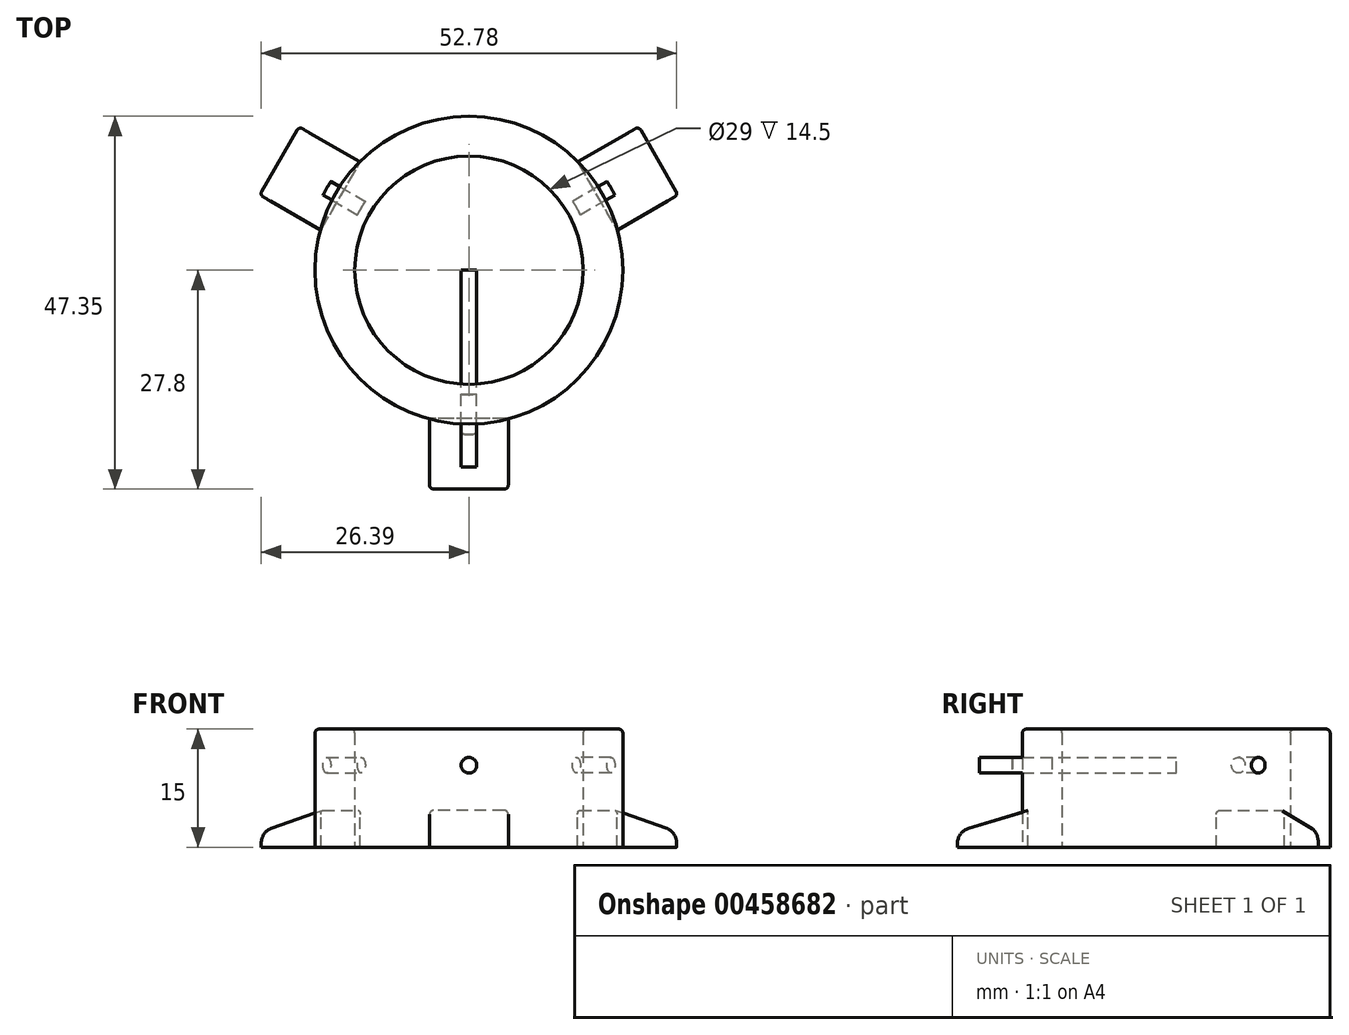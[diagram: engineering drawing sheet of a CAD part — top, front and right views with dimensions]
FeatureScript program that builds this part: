
annotation { "Feature Type Name" : "Feature", "Feature Type Description" : "" }
export const myFeature = defineFeature(function(context is Context, id is Id, definition is map)
    precondition{}
    {
        {
            var Q0;
            Q0=qCreatedBy(makeId("Top.planeOp"),FACE);
            var sketch = newSketch(context, id + "F0", { "sketchPlane" : qUnion([Q0])});
            skCircle(sketch, "E0", {"center": v(0, 0) * mm, "radius": 14.5 * mm});
            skCircle(sketch, "E1", {"center": v(0, 0) * mm, "radius": 19.55 * mm});
            skSolve(sketch);
        }
        {
            var Q0;
            Q0 = qSketchRegion(id + "F0", true);
            extrude(context, id + "F1", {"entities" : qUnion([Q0]), "depth" : 15 * mm});
        }
        {
            var Q0;
            Q0=qCreatedBy(makeId("Front.planeOp"),FACE);
            var sketch = newSketch(context, id + "F2", { "sketchPlane" : qUnion([Q0])});
            skCircle(sketch, "E2", {"center": v(0, 10.41) * mm, "radius": 1 * mm});
            skSolve(sketch);
        }
        {
            var Q0;
            Q0 = qSketchRegion(id + "F2", true);
            extrude(context, id + "F3", {"entities" : qUnion([Q0]), "depth" : 25 * mm});
        }
        {
            var Q0;
            Q0=makeQuery(id+"F1.opExtrude","SWEPT_BODY",BODY,{"disambiguationData":[OSD([sQuery(id+"F0.wireOp",EDGE,"E0"),sQuery(id+"F0.wireOp",EDGE,"E1")])]});
            var Q1;
            Q1=makeQuery(id+"F3.opExtrude","SWEPT_BODY",BODY,{"disambiguationData":[OSD([sQuery(id+"F2.wireOp",EDGE,"E2")])]});
            booleanBodies(context, id + "F4", {"operationType" : BooleanOperationType.INTERSECTION, "tools" : qUnion([Q0, Q1]), "keepTools" : true});
        }
        {
            var Q0;
            Q0=makeQuery(id+"F4.opBoolean","INTERSECT",BODY,{"derivedFrom":[makeQuery(id+"F1.opExtrude","SWEPT_BODY",BODY,{"disambiguationData":[OSD([sQuery(id+"F0.wireOp",EDGE,"E0"),sQuery(id+"F0.wireOp",EDGE,"E1")])]}),makeQuery(id+"F3.opExtrude","SWEPT_BODY",BODY,{"disambiguationData":[OSD([sQuery(id+"F2.wireOp",EDGE,"E2")])]})]});
            transform(context, id + "F5", {"entities" : qUnion([Q0]), "transformType" : TransformType.TRANSLATION_3D, "dx" : 0 * mm, "dy" : -1.3 * mm, "dz" : 0 * mm, "makeCopy" : false});
        }
        {
            var Q0;
            Q0=makeQuery(id+"F4.opBoolean","INTERSECT",BODY,{"derivedFrom":[makeQuery(id+"F1.opExtrude","SWEPT_BODY",BODY,{"disambiguationData":[OSD([sQuery(id+"F0.wireOp",EDGE,"E0"),sQuery(id+"F0.wireOp",EDGE,"E1")])]}),makeQuery(id+"F3.opExtrude","SWEPT_BODY",BODY,{"disambiguationData":[OSD([sQuery(id+"F2.wireOp",EDGE,"E2")])]})]});
            var Q1;
            Q1=makeQuery(id+"F1.opExtrude","SWEPT_FACE",FACE,{"disambiguationData":[OSD([sQuery(id+"F0.wireOp",EDGE,"E1")])]});
            circularPattern(context, id + "F6", {"entities" : qUnion([Q0]), "axis" : qUnion([Q1]), "angle" : 360 * degree, "instanceCount" : 3, "equalSpace" : true});
        }
        {
            var Q0;
            Q0=qCreatedBy(makeId("Right.planeOp"),FACE);
            var sketch = newSketch(context, id + "F7", { "sketchPlane" : qUnion([Q0])});
            skLineSegment(sketch, "E3", {"start": v(-18.83, 4.67) * mm, "end": v(-27.8, 1.95) * mm});
            skLineSegment(sketch, "E4", {"start": v(-27.8, 1.95) * mm, "end": v(-27.8, 0) * mm});
            skLineSegment(sketch, "E5", {"start": v(-27.8, 0) * mm, "end": v(-18.83, 0) * mm});
            skLineSegment(sketch, "E6", {"start": v(-18.83, 0) * mm, "end": v(-18.83, 4.67) * mm});
            skSolve(sketch);
        }
        {
            var Q0;
            Q0 = qSketchRegion(id + "F7", true);
            extrude(context, id + "F8", {"entities" : qUnion([Q0]), "endBound" : BoundingType.SYMMETRIC, "depth" : 10 * mm});
        }
        {
            var Q0;
            Q0=makeQuery(id+"F8.opExtrude","SWEPT_EDGE",EDGE,{"disambiguationData":[OSD([sQuery(id+"F7.wireOp",EDGE,"E3"),sQuery(id+"F7.wireOp",EDGE,"E4")])]});
            fillet(context, id + "F9", {"entities" : qUnion([Q0]), "radius" : 2 * mm, "tangentPropagation" : true, "allowEdgeOverflow" : false});
        }
        {
            var Q0;
            Q0=makeQuery(id+"F8.opExtrude","CAP_EDGE",EDGE,{"disambiguationData":[OSD([sQuery(id+"F7.wireOp",EDGE,"E3")])],"isStart":true});
            var Q1;
            Q1=makeQuery(id+"F8.opExtrude","CAP_EDGE",EDGE,{"disambiguationData":[OSD([sQuery(id+"F7.wireOp",EDGE,"E3")])],"isStart":false});
            var Q2;
            Q2=makeQuery(id+"F1.opExtrude","CAP_EDGE",EDGE,{"disambiguationData":[OSD([sQuery(id+"F0.wireOp",EDGE,"E1")])],"isStart":false});
            var Q3;
            Q3=makeQuery(id+"F1.opExtrude","CAP_EDGE",EDGE,{"disambiguationData":[OSD([sQuery(id+"F0.wireOp",EDGE,"E0")])],"isStart":false});
            fillet(context, id + "F10", {"entities" : qUnion([Q0, Q1, Q2, Q3]), "radius" : .5 * mm, "tangentPropagation" : true, "allowEdgeOverflow" : false});
        }
        {
            var Q0;
            Q0=makeQuery(id+"F8.opExtrude","SWEPT_BODY",BODY,{"disambiguationData":[OSD([sQuery(id+"F7.wireOp",EDGE,"E3"),sQuery(id+"F7.wireOp",EDGE,"E4"),sQuery(id+"F7.wireOp",EDGE,"E5"),sQuery(id+"F7.wireOp",EDGE,"E6")])]});
            var Q1;
            Q1=makeQuery(id+"F1.opExtrude","SWEPT_FACE",FACE,{"disambiguationData":[OSD([sQuery(id+"F0.wireOp",EDGE,"E1")])]});
            circularPattern(context, id + "F11", {"entities" : qUnion([Q0]), "axis" : qUnion([Q1]), "angle" : 360 * degree, "instanceCount" : 3, "equalSpace" : true});
        }
    });
